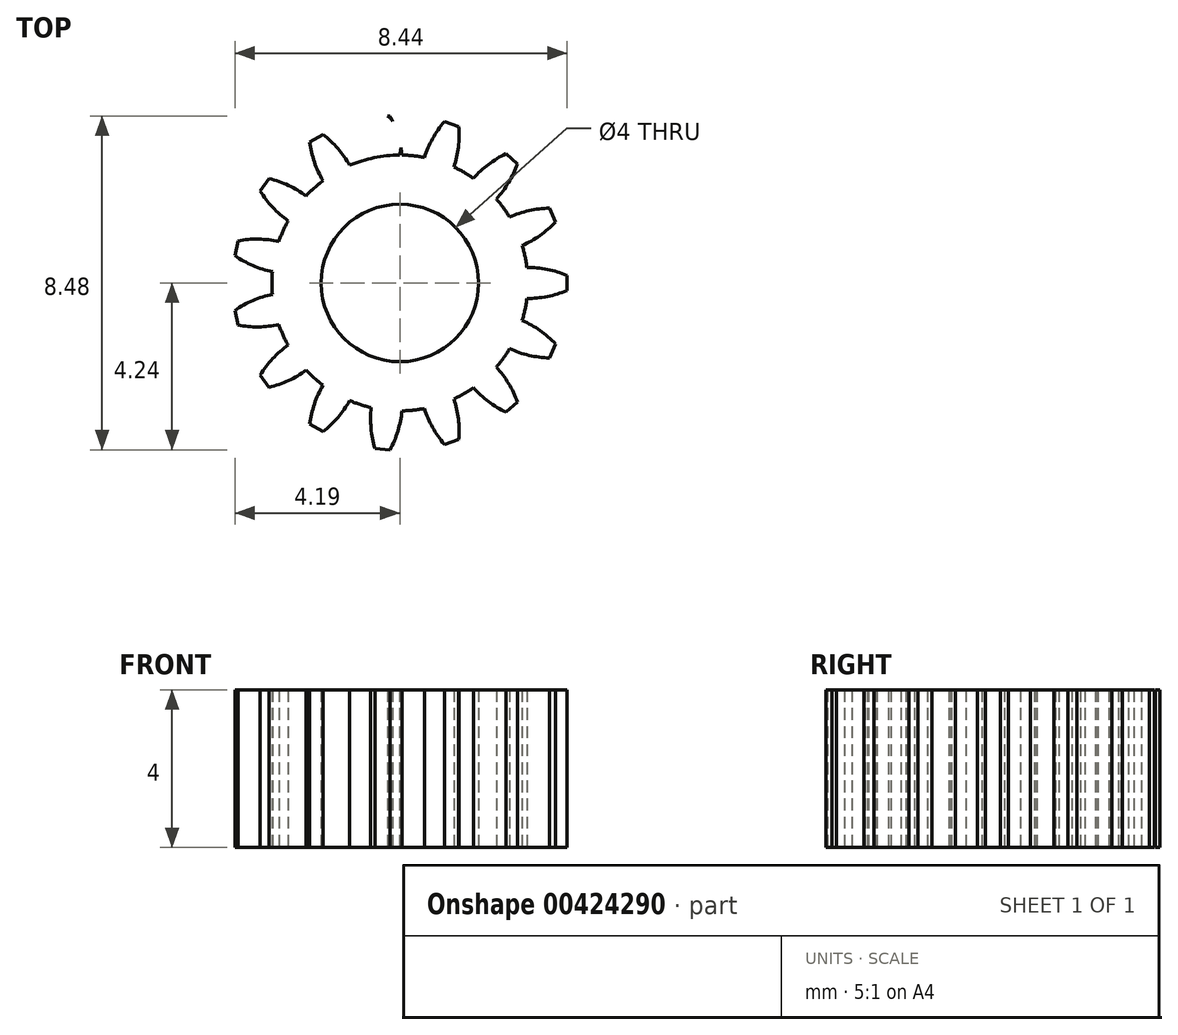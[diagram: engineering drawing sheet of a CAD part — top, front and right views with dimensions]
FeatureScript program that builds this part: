
annotation { "Feature Type Name" : "Feature", "Feature Type Description" : "" }
export const myFeature = defineFeature(function(context is Context, id is Id, definition is map)
    precondition{}
    {
        {
            assignVariable(context, id + "F0", {"name" : "GearDepth", "anyValue" : 4});
        }
        {
            var Q0;
            Q0=qCreatedBy(makeId("Top.planeOp"),FACE);
            var sketch = newSketch(context, id + "F1", { "sketchPlane" : qUnion([Q0])});
            skCircle(sketch, "E0", {"center": v(0, 0) * mm, "radius": 3.25 * mm});
            skCircle(sketch, "E1", {"center": v(0, 0) * mm, "radius": 3.75 * mm, "construction": true});
            skCircle(sketch, "E2", {"center": v(0, 0) * mm, "radius": 4.25 * mm, "construction": true});
            skLineSegment(sketch, "E3", {"start": v(0, 0) * mm, "end": v(0, 17.6) * mm, "construction": true});
            skLineSegment(sketch, "E4", {"start": v(0, 0) * mm, "end": v(-1.89, 17.95) * mm, "construction": true});
            skLineSegment(sketch, "E5", {"start": v(0, 3.75) * mm, "end": v(-10.54, 3.75) * mm, "construction": true});
            skLineSegment(sketch, "E6", {"start": v(0, 3.75) * mm, "end": v(-10.6, 1.03) * mm, "construction": true});
            skCircle(sketch, "E7", {"center": v(0, 3.75) * mm, "radius": 0.94 * mm, "construction": true});
            skCircle(sketch, "E8", {"center": v(-0.9, 3.52) * mm, "radius": 0.94 * mm, "construction": true});
            skArc(sketch, "E9", {"start": v(-1.82, 3.75) * mm, "mid": v(-0.02, 3.23) * mm, "end": v(-1.78, 3.86) * mm});
            skArc(sketch, "E10.trimOffspring", {"start": v(0.05, 3.25) * mm, "mid": v(-0.05, 3.76) * mm, "end": v(-0.25, 4.24) * mm});
            skArc(sketch, "E11.MirrorCS", {"start": v(-0.73, 3.17) * mm, "mid": v(-0.73, 3.69) * mm, "end": v(-0.64, 4.2) * mm});
            skLineSegment(sketch, "E12", {"start": v(-0.64, 4.2) * mm, "end": v(-0.25, 4.24) * mm});
            skArc(sketch, "E13.1.0", {"start": v(-1.27, 3) * mm, "mid": v(-1.58, 3.42) * mm, "end": v(-1.96, 3.77) * mm});
            skLineSegment(sketch, "E13.1.1", {"start": v(-2.29, 3.58) * mm, "end": v(-1.96, 3.77) * mm});
            skArc(sketch, "E13.1.2", {"start": v(-1.95, 2.6) * mm, "mid": v(-2.17, 3.07) * mm, "end": v(-2.29, 3.58) * mm});
            skArc(sketch, "E13.2.0", {"start": v(-2.38, 2.21) * mm, "mid": v(-2.83, 2.48) * mm, "end": v(-3.32, 2.65) * mm});
            skLineSegment(sketch, "E13.2.1", {"start": v(-3.55, 2.34) * mm, "end": v(-3.32, 2.65) * mm});
            skArc(sketch, "E13.2.2", {"start": v(-2.84, 1.58) * mm, "mid": v(-3.23, 1.92) * mm, "end": v(-3.55, 2.34) * mm});
            skArc(sketch, "E13.3.0", {"start": v(-3.07, 1.05) * mm, "mid": v(-3.6, 1.12) * mm, "end": v(-4.11, 1.07) * mm});
            skLineSegment(sketch, "E13.3.1", {"start": v(-4.2, 0.7) * mm, "end": v(-4.11, 1.07) * mm});
            skArc(sketch, "E13.3.2", {"start": v(-3.24, 0.29) * mm, "mid": v(-3.74, 0.44) * mm, "end": v(-4.2, 0.7) * mm});
            skArc(sketch, "E13.4.0", {"start": v(-3.24, -0.29) * mm, "mid": v(-3.74, -0.44) * mm, "end": v(-4.2, -0.7) * mm});
            skLineSegment(sketch, "E13.4.1", {"start": v(-4.11, -1.07) * mm, "end": v(-4.2, -0.7) * mm});
            skArc(sketch, "E13.4.2", {"start": v(-3.07, -1.05) * mm, "mid": v(-3.6, -1.12) * mm, "end": v(-4.11, -1.07) * mm});
            skArc(sketch, "E13.5.0", {"start": v(-2.84, -1.58) * mm, "mid": v(-3.23, -1.92) * mm, "end": v(-3.55, -2.34) * mm});
            skLineSegment(sketch, "E13.5.1", {"start": v(-3.32, -2.65) * mm, "end": v(-3.55, -2.34) * mm});
            skArc(sketch, "E13.5.2", {"start": v(-2.38, -2.21) * mm, "mid": v(-2.83, -2.48) * mm, "end": v(-3.32, -2.65) * mm});
            skArc(sketch, "E13.6.0", {"start": v(-1.95, -2.6) * mm, "mid": v(-2.17, -3.07) * mm, "end": v(-2.29, -3.58) * mm});
            skLineSegment(sketch, "E13.6.1", {"start": v(-1.96, -3.77) * mm, "end": v(-2.29, -3.58) * mm});
            skArc(sketch, "E13.6.2", {"start": v(-1.27, -3) * mm, "mid": v(-1.58, -3.42) * mm, "end": v(-1.96, -3.77) * mm});
            skArc(sketch, "E13.7.0", {"start": v(-0.73, -3.17) * mm, "mid": v(-0.73, -3.69) * mm, "end": v(-0.64, -4.2) * mm});
            skLineSegment(sketch, "E13.7.1", {"start": v(-0.25, -4.24) * mm, "end": v(-0.64, -4.2) * mm});
            skArc(sketch, "E13.7.2", {"start": v(0.05, -3.25) * mm, "mid": v(-0.05, -3.76) * mm, "end": v(-0.25, -4.24) * mm});
            skArc(sketch, "E13.8.0", {"start": v(0.62, -3.19) * mm, "mid": v(0.83, -3.67) * mm, "end": v(1.13, -4.1) * mm});
            skLineSegment(sketch, "E13.8.1", {"start": v(1.5, -3.98) * mm, "end": v(1.13, -4.1) * mm});
            skArc(sketch, "E13.8.2", {"start": v(1.37, -2.95) * mm, "mid": v(1.48, -3.46) * mm, "end": v(1.5, -3.98) * mm});
            skArc(sketch, "E13.9.0", {"start": v(1.87, -2.66) * mm, "mid": v(2.25, -3.01) * mm, "end": v(2.7, -3.28) * mm});
            skLineSegment(sketch, "E13.9.1", {"start": v(2.98, -3.03) * mm, "end": v(2.7, -3.28) * mm});
            skArc(sketch, "E13.9.2", {"start": v(2.45, -2.14) * mm, "mid": v(2.76, -2.55) * mm, "end": v(2.98, -3.03) * mm});
            skArc(sketch, "E13.10.0", {"start": v(2.79, -1.67) * mm, "mid": v(3.28, -1.84) * mm, "end": v(3.8, -1.9) * mm});
            skLineSegment(sketch, "E13.10.1", {"start": v(3.96, -1.55) * mm, "end": v(3.8, -1.9) * mm});
            skArc(sketch, "E13.10.2", {"start": v(3.1, -0.95) * mm, "mid": v(3.56, -1.2) * mm, "end": v(3.96, -1.55) * mm});
            skArc(sketch, "E13.11.0", {"start": v(3.23, -0.4) * mm, "mid": v(3.75, -0.34) * mm, "end": v(4.25, -0.2) * mm});
            skLineSegment(sketch, "E13.11.1", {"start": v(4.25, 0.2) * mm, "end": v(4.25, -0.2) * mm});
            skArc(sketch, "E13.11.2", {"start": v(3.23, 0.4) * mm, "mid": v(3.75, 0.34) * mm, "end": v(4.25, 0.2) * mm});
            skArc(sketch, "E13.12.0", {"start": v(3.1, 0.95) * mm, "mid": v(3.56, 1.2) * mm, "end": v(3.96, 1.55) * mm});
            skLineSegment(sketch, "E13.12.1", {"start": v(3.8, 1.9) * mm, "end": v(3.96, 1.55) * mm});
            skArc(sketch, "E13.12.2", {"start": v(2.79, 1.67) * mm, "mid": v(3.28, 1.84) * mm, "end": v(3.8, 1.9) * mm});
            skArc(sketch, "E13.13.0", {"start": v(2.45, 2.14) * mm, "mid": v(2.76, 2.55) * mm, "end": v(2.98, 3.03) * mm});
            skLineSegment(sketch, "E13.13.1", {"start": v(2.7, 3.28) * mm, "end": v(2.98, 3.03) * mm});
            skArc(sketch, "E13.13.2", {"start": v(1.87, 2.66) * mm, "mid": v(2.25, 3.01) * mm, "end": v(2.7, 3.28) * mm});
            skArc(sketch, "E13.14.0", {"start": v(1.37, 2.95) * mm, "mid": v(1.48, 3.46) * mm, "end": v(1.5, 3.98) * mm});
            skLineSegment(sketch, "E13.14.1", {"start": v(1.13, 4.1) * mm, "end": v(1.5, 3.98) * mm});
            skArc(sketch, "E13.14.2", {"start": v(0.62, 3.19) * mm, "mid": v(0.83, 3.67) * mm, "end": v(1.13, 4.1) * mm});
            skCircle(sketch, "E14", {"center": v(0, 0) * mm, "radius": 2 * mm});
            skSolve(sketch);
        }
        {
            var Q0;
            {var subQ0=sQuery(id+"F1.wireOp",EDGE,"E10.trimOffspring");Q0=makeQuery(id+"F1.imprint","IMPRINT",FACE,{"disambiguationData":[TD([[makeQuery(id+"F1.imprint","IMPRINT",EDGE,{"derivedFrom":subQ0}),1.0]])]});}
            var Q1;
            {var subQ0=sQuery(id+"F1.wireOp",EDGE,"E0");var subQ1=makeQuery(id+"F1.imprint","INTERSECT",VERTEX,{"derivedFrom":[subQ0,sQuery(id+"F1.wireOp",EDGE,"E10.trimOffspring")]});Q1=makeQuery(id+"F1.imprint","IMPRINT",FACE,{"disambiguationData":[TD([[makeQuery(id+"F1.imprint","IMPRINT",EDGE,{"disambiguationData":[TD([[subQ1,-1.0]])],"derivedFrom":subQ0}),1.0]])]});}
            var Q2;
            {var subQ0=sQuery(id+"F1.wireOp",EDGE,"E13.1.0");Q2=makeQuery(id+"F1.imprint","IMPRINT",FACE,{"disambiguationData":[TD([[makeQuery(id+"F1.imprint","IMPRINT",EDGE,{"derivedFrom":subQ0}),1.0]])]});}
            var Q3;
            {var subQ0=sQuery(id+"F1.wireOp",EDGE,"E13.2.0");Q3=makeQuery(id+"F1.imprint","IMPRINT",FACE,{"disambiguationData":[TD([[makeQuery(id+"F1.imprint","IMPRINT",EDGE,{"derivedFrom":subQ0}),1.0]])]});}
            var Q4;
            {var subQ0=sQuery(id+"F1.wireOp",EDGE,"E13.3.0");Q4=makeQuery(id+"F1.imprint","IMPRINT",FACE,{"disambiguationData":[TD([[makeQuery(id+"F1.imprint","IMPRINT",EDGE,{"derivedFrom":subQ0}),1.0]])]});}
            var Q5;
            {var subQ0=sQuery(id+"F1.wireOp",EDGE,"E13.4.0");Q5=makeQuery(id+"F1.imprint","IMPRINT",FACE,{"disambiguationData":[TD([[makeQuery(id+"F1.imprint","IMPRINT",EDGE,{"derivedFrom":subQ0}),1.0]])]});}
            var Q6;
            {var subQ0=sQuery(id+"F1.wireOp",EDGE,"E13.5.0");Q6=makeQuery(id+"F1.imprint","IMPRINT",FACE,{"disambiguationData":[TD([[makeQuery(id+"F1.imprint","IMPRINT",EDGE,{"derivedFrom":subQ0}),1.0]])]});}
            var Q7;
            {var subQ0=sQuery(id+"F1.wireOp",EDGE,"E13.6.0");Q7=makeQuery(id+"F1.imprint","IMPRINT",FACE,{"disambiguationData":[TD([[makeQuery(id+"F1.imprint","IMPRINT",EDGE,{"derivedFrom":subQ0}),1.0]])]});}
            var Q8;
            {var subQ0=sQuery(id+"F1.wireOp",EDGE,"E13.7.0");Q8=makeQuery(id+"F1.imprint","IMPRINT",FACE,{"disambiguationData":[TD([[makeQuery(id+"F1.imprint","IMPRINT",EDGE,{"derivedFrom":subQ0}),1.0]])]});}
            var Q9;
            {var subQ0=sQuery(id+"F1.wireOp",EDGE,"E13.8.0");Q9=makeQuery(id+"F1.imprint","IMPRINT",FACE,{"disambiguationData":[TD([[makeQuery(id+"F1.imprint","IMPRINT",EDGE,{"derivedFrom":subQ0}),1.0]])]});}
            var Q10;
            {var subQ0=sQuery(id+"F1.wireOp",EDGE,"E13.9.0");Q10=makeQuery(id+"F1.imprint","IMPRINT",FACE,{"disambiguationData":[TD([[makeQuery(id+"F1.imprint","IMPRINT",EDGE,{"derivedFrom":subQ0}),1.0]])]});}
            var Q11;
            {var subQ0=sQuery(id+"F1.wireOp",EDGE,"E13.10.0");Q11=makeQuery(id+"F1.imprint","IMPRINT",FACE,{"disambiguationData":[TD([[makeQuery(id+"F1.imprint","IMPRINT",EDGE,{"derivedFrom":subQ0}),1.0]])]});}
            var Q12;
            {var subQ0=sQuery(id+"F1.wireOp",EDGE,"E13.11.0");Q12=makeQuery(id+"F1.imprint","IMPRINT",FACE,{"disambiguationData":[TD([[makeQuery(id+"F1.imprint","IMPRINT",EDGE,{"derivedFrom":subQ0}),1.0]])]});}
            var Q13;
            {var subQ0=sQuery(id+"F1.wireOp",EDGE,"E13.12.0");Q13=makeQuery(id+"F1.imprint","IMPRINT",FACE,{"disambiguationData":[TD([[makeQuery(id+"F1.imprint","IMPRINT",EDGE,{"derivedFrom":subQ0}),1.0]])]});}
            var Q14;
            {var subQ0=sQuery(id+"F1.wireOp",EDGE,"E13.13.0");Q14=makeQuery(id+"F1.imprint","IMPRINT",FACE,{"disambiguationData":[TD([[makeQuery(id+"F1.imprint","IMPRINT",EDGE,{"derivedFrom":subQ0}),1.0]])]});}
            var Q15;
            {var subQ0=sQuery(id+"F1.wireOp",EDGE,"E13.14.0");Q15=makeQuery(id+"F1.imprint","IMPRINT",FACE,{"disambiguationData":[TD([[makeQuery(id+"F1.imprint","IMPRINT",EDGE,{"derivedFrom":subQ0}),1.0]])]});}
            var Q16;
            {var subQ0=sQuery(id+"F1.wireOp",EDGE,"E13.15.0");Q16=makeQuery(id+"F1.imprint","IMPRINT",FACE,{"disambiguationData":[TD([[makeQuery(id+"F1.imprint","IMPRINT",EDGE,{"derivedFrom":subQ0}),1.0]])]});}
            var Q17;
            {var subQ0=sQuery(id+"F1.wireOp",EDGE,"E13.16.0");Q17=makeQuery(id+"F1.imprint","IMPRINT",FACE,{"disambiguationData":[TD([[makeQuery(id+"F1.imprint","IMPRINT",EDGE,{"derivedFrom":subQ0}),1.0]])]});}
            var Q18;
            {var subQ0=sQuery(id+"F1.wireOp",EDGE,"E13.17.0");Q18=makeQuery(id+"F1.imprint","IMPRINT",FACE,{"disambiguationData":[TD([[makeQuery(id+"F1.imprint","IMPRINT",EDGE,{"derivedFrom":subQ0}),1.0]])]});}
            var Q19;
            {var subQ0=sQuery(id+"F1.wireOp",EDGE,"E13.18.0");Q19=makeQuery(id+"F1.imprint","IMPRINT",FACE,{"disambiguationData":[TD([[makeQuery(id+"F1.imprint","IMPRINT",EDGE,{"derivedFrom":subQ0}),1.0]])]});}
            var Q20;
            {var subQ0=sQuery(id+"F1.wireOp",EDGE,"E13.19.0");Q20=makeQuery(id+"F1.imprint","IMPRINT",FACE,{"disambiguationData":[TD([[makeQuery(id+"F1.imprint","IMPRINT",EDGE,{"derivedFrom":subQ0}),1.0]])]});}
            var Q21;
            {var subQ0=sQuery(id+"F1.wireOp",EDGE,"E13.1.1");Q21=makeQuery(id+"F1.imprint","IMPRINT",FACE,{"disambiguationData":[TD([[makeQuery(id+"F1.imprint","IMPRINT",EDGE,{"derivedFrom":subQ0}),-1.0]])]});}
            var Q22;
            {var subQ0=sQuery(id+"F1.wireOp",EDGE,"E0");var subQ1=makeQuery(id+"F1.imprint","INTERSECT",VERTEX,{"derivedFrom":[subQ0,sQuery(id+"F1.wireOp",EDGE,"E11.MirrorCS")]});Q22=makeQuery(id+"F1.imprint","IMPRINT",FACE,{"disambiguationData":[TD([[makeQuery(id+"F1.imprint","IMPRINT",EDGE,{"disambiguationData":[TD([[subQ1,1.0]])],"derivedFrom":subQ0}),1.0]])]});}
            var Q23;
            {var subQ8=sQuery(id+"F1.wireOp",EDGE,"E11.MirrorCS");Q23=makeQuery(id+"F1.imprint","IMPRINT",FACE,{"disambiguationData":[TD([[makeQuery(id+"F1.imprint","IMPRINT",EDGE,{"derivedFrom":subQ8}),-1.0]])]});}
            var Q24;
            Q24=sQuery(id+"F1.wireOp",EDGE,"E0");
            var Q25;
            Q25=sQuery(id+"F1.wireOp",EDGE,"E10.trimOffspring");
            var Q26;
            Q26=sQuery(id+"F1.wireOp",EDGE,"E12");
            var Q27;
            Q27=sQuery(id+"F1.wireOp",EDGE,"E11.MirrorCS");
            extrude(context, id + "F2", {"entities" : qUnion([Q0, Q1, Q2, Q3, Q4, Q5, Q6, Q7, Q8, Q9, Q10, Q11, Q12, Q13, Q14, Q15, Q16, Q17, Q18, Q19, Q20, Q21, Q22, Q23]), "surfaceEntities" : qUnion([Q24, Q25, Q26, Q27]), "depth" : (getVariable(context, 'GearDepth')) * mm, "offsetDistance" : 25 * mm});
        }
    });
